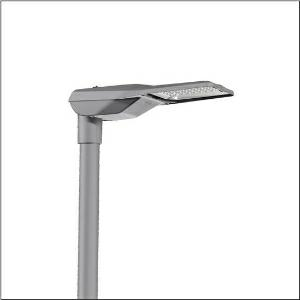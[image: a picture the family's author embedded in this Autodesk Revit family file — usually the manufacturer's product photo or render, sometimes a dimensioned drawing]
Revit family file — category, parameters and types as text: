
# Revit family: streetlight_sl_21_mini___st0_5a_5xe2b43s08jb_3299
name_source: partatom
category: Lighting Fixtures
units: mm (PartAtom-declared; Revit-internal decimal feet)

## family parameters
Cut with Voids When Loaded = No
Host = Face
Light Source = No
Part Type = Normal
Room Calculation Point = No
Round Connector Dimension = Use Diameter
Shared = No

## types (1)
- --- (1 x LED, 13500 lm, 88.6 W, 4000K)
    Apparent Load = 89 VA
    CIE Flux Codes = 43 76 97 100 100
    Color Rendering = 70
    Color Temperature = 4000K
    Default Elevation = 1800 mm
    Description = Streetlight SL 21 mini, mast luminaire, primary light control with lens, of PMMA, primary optical cover: cover, of toughened safety glass, transparent, light distribution: ST0.5a, light emission: direct distribution, primary light characteristic: asymmetric, installation type: side-entry, post-top, LED, High Power LED, rated luminous flux: 13.500lm, luminous efficacy: 152lm/W, light colour: 740, colour temperature: 4000K, control gear: D4i, control: overheat protection, constant luminous flux control, time-dependent luminous flux control, flexible luminous flux parameterisation, pre-setting: logarithmic dimming characteristic, mains connection: 220..240V, AC, 50/60Hz, start of lifetime: 89W, end of service life: 92W, reduction: 41W, luminaire housing, of diecast aluminium, powder-coated, Siteco® metallic grey (DB 702S), corrosivity category C5 mid according to DIN EN ISO 12944, please order mast flange separately, inclination adjustable: 0°, 5°, 10°, 15°, sealing non-destructively replaceable, multi-level sealing system, length: 628mm, width: 235mm, height: 110mm, mast flange for spigot size: 42mm (side-entry): 5XC10008XM4, 60/48mm (side-entry/post-top): 5XC10108XM2, 76/60mm (side-entry/post-top): 5XC10108XM1, mounting height: 4..8m, Smart Interface above, protection rating (complete): IP66, insulation class (complete): insulation class II (safety insulation), certification: CE, ENEC, ENEC+, VDE, impact resistance: IK10, permissible operating ambient temperature for outdoor applications: -40..+50°C, standard-compliant lighting for roads and squares, packaging unit: 1 piece

Light Distribution: ST0.5a
    Height = 110 mm
    Lamp = 1 x LED
    Lamp Light Flux = 13500 lm
    Lamp Power = 88.6 W
    Lamp count = 1
    Length = 625 mm
    Luminous efficacy = 152 lm/W
    Manufacturer = Siteco
    ModVariant = No
    Model = 5XE2B43S08JB
    Number of Poles = 1
    OnlyDefault = Yes
    Power Factor = 1
    Product Name = Streetlight SL 21 mini | ST0.5a
    Product group = mast luminaire | pylon top
    ProductGroupID = 6100
    Protection Class = Protection class II
    Protection Degree = IP 66
    RLX_Detail_Level = 1
    RLX_Emergency_Light_Flux = 0 lm
    RLX_Emergency_Type = 0
    RLX_Emergency_Type_DB = No
    RlxData = <blob elided: 37389 chars, md5=4ced045d>
    Socket = socket
    Standby Power = 0 W
    System Light Flux = 13500 lm
    System Power = 89 W
    Type Comments = factory setting: luminous flux: 100 % | dim-lin: 254 | 915 mA
    Type Image = l_1003515.jpg
    URL = http://relux.com
    VarID = @adj_032275
    Voltage = 0 V
    Weight = 0.00 kg
    Width = 234 mm

## geometry (parser evidence)
native form markers: Blend x4, Sweep x9
no freeform markers — native parametric forms only
